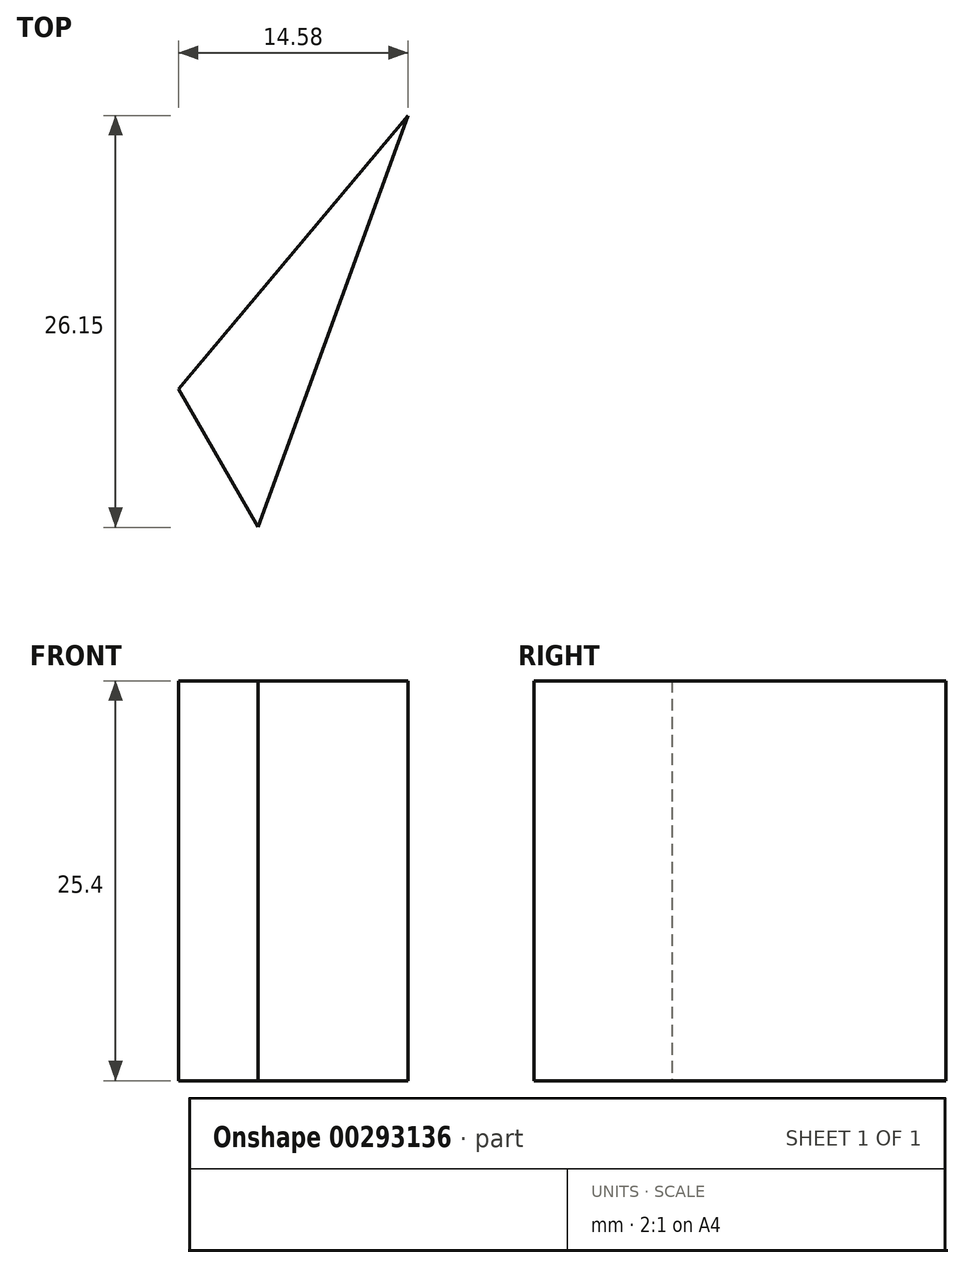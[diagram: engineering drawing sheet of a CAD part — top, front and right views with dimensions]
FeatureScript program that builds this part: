
annotation { "Feature Type Name" : "Feature", "Feature Type Description" : "" }
export const myFeature = defineFeature(function(context is Context, id is Id, definition is map)
    precondition{}
    {
        {
            var Q0;
            Q0=qCreatedBy(makeId("Top.planeOp"),FACE);
            var sketch = newSketch(context, id + "F0", { "sketchPlane" : qUnion([Q0])});
            skLineSegment(sketch, "E0", {"start": v(-7.76, 0) * mm, "end": v(25.4, 0) * mm});
            skLineSegment(sketch, "E1", {"start": v(25.4, 0) * mm, "end": v(0, 44) * mm});
            skLineSegment(sketch, "E2", {"start": v(25.4, 0) * mm, "end": v(8.82, 94.02) * mm});
            skLineSegment(sketch, "E3", {"start": v(0, 44) * mm, "end": v(-7.76, 0) * mm});
            skLineSegment(sketch, "E4", {"start": v(0, 44) * mm, "end": v(8.82, 94.02) * mm});
            skLineSegment(sketch, "E5", {"start": v(-7.76, 0) * mm, "end": v(14.58, 61.37) * mm});
            skLineSegment(sketch, "E6", {"start": v(14.58, 61.37) * mm, "end": v(0, 44) * mm});
            skSolve(sketch);
        }
        {
            var Q0;
            {var subQ0=sQuery(id+"F0.wireOp",EDGE,"E6");Q0=makeQuery(id+"F0.imprint","IMPRINT",FACE,{"disambiguationData":[TD([[makeQuery(id+"F0.imprint","IMPRINT",EDGE,{"derivedFrom":subQ0}),1.0]])]});}
            extrude(context, id + "F1", {"entities" : qUnion([Q0]), "depth" : 25.4 * mm});
        }
    });
